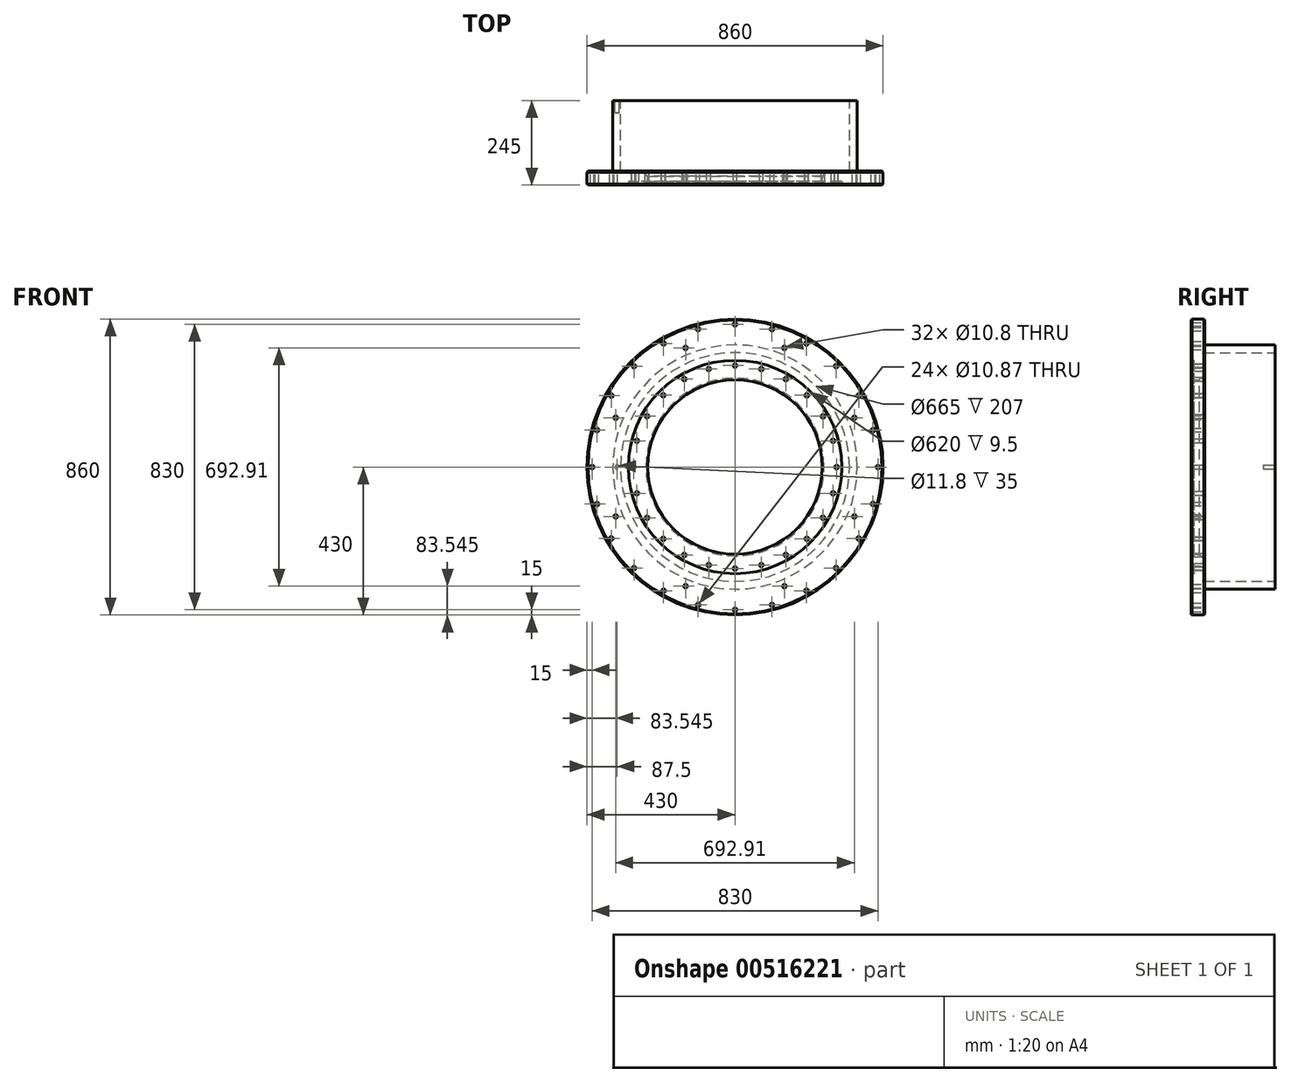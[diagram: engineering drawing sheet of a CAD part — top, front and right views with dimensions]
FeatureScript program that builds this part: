
annotation { "Feature Type Name" : "Feature", "Feature Type Description" : "" }
export const myFeature = defineFeature(function(context is Context, id is Id, definition is map)
    precondition{}
    {
        {
            var Q0;
            Q0=qCreatedBy(makeId("Front.planeOp"),FACE);
            var sketch = newSketch(context, id + "F0", { "sketchPlane" : qUnion([Q0])});
            skCircle(sketch, "E0", {"center": v(0, 0) * mm, "radius": 430 * mm});
            skCircle(sketch, "E1", {"center": v(0, 0) * mm, "radius": 250 * mm});
            skSolve(sketch);
        }
        {
            var Q0;
            Q0 = qSketchRegion(id + "F0", true);
            extrude(context, id + "F1", {"entities" : qUnion([Q0]), "depth" : 245 * mm, "offsetDistance" : 25 * mm});
        }
        {
            var Q0;
            Q0=makeQuery(id+"F1.opExtrude","CAP_FACE",FACE,{"disambiguationData":[OSD([sQuery(id+"F0.wireOp",EDGE,"E0"),sQuery(id+"F0.wireOp",EDGE,"E1")])],"isStart":true});
            var sketch = newSketch(context, id + "F2", { "sketchPlane" : qUnion([Q0])});
            skCircle(sketch, "E2", {"center": v(0, 0) * mm, "radius": 355 * mm});
            skCircle(sketch, "E3", {"center": v(0, 0) * mm, "radius": 514.3 * mm});
            skSolve(sketch);
        }
        {
            var Q0;
            Q0=makeQuery(id+"F2.imprint","IMPRINT",FACE,{"disambiguationData":[TD([[makeQuery(id+"F2.imprint","IMPRINT",EDGE,{"derivedFrom":sQuery(id+"F2.wireOp",EDGE,"E2")}),-1.0]])]});
            var Q1;
            Q1=makeQuery(id+"F2.imprint","IMPRINT",FACE,{"disambiguationData":[TD([[makeQuery(id+"F2.imprint","IMPRINT",EDGE,{"derivedFrom":sQuery(id+"F2.wireOp",EDGE,"E3")}),1.0]])]});
            extrude(context, id + "F3", {"entities" : qUnion([Q0, Q1]), "operationType" : NewBodyOperationType.REMOVE, "oppositeDirection" : true, "depth" : 205 * mm, "offsetDistance" : 25 * mm});
        }
        {
            var Q0;
            Q0=makeQuery(id+"F1.opExtrude","CAP_FACE",FACE,{"disambiguationData":[OSD([sQuery(id+"F0.wireOp",EDGE,"E0"),sQuery(id+"F0.wireOp",EDGE,"E1")])],"isStart":true});
            var sketch = newSketch(context, id + "F4", { "sketchPlane" : qUnion([Q0])});
            skCircle(sketch, "E4", {"center": v(0, 0) * mm, "radius": 332.5 * mm});
            skCircle(sketch, "E5", {"center": v(0, 0) * mm, "radius": 222.4 * mm});
            skSolve(sketch);
        }
        {
            var Q0;
            Q0=makeQuery(id+"F4.imprint","IMPRINT",FACE,{"disambiguationData":[TD([[makeQuery(id+"F4.imprint","IMPRINT",EDGE,{"derivedFrom":sQuery(id+"F4.wireOp",EDGE,"E5")}),-1.0]])]});
            var Q1;
            Q1=makeQuery(id+"F4.imprint","IMPRINT",FACE,{"disambiguationData":[TD([[makeQuery(id+"F4.imprint","IMPRINT",EDGE,{"derivedFrom":sQuery(id+"F4.wireOp",EDGE,"E4")}),1.0]])]});
            extrude(context, id + "F5", {"entities" : qUnion([Q0, Q1]), "operationType" : NewBodyOperationType.REMOVE, "oppositeDirection" : true, "depth" : 210 * mm, "offsetDistance" : 25 * mm});
        }
        {
            var Q0;
            Q0=makeQuery(id+"F1.opExtrude","CAP_FACE",FACE,{"disambiguationData":[OSD([sQuery(id+"F0.wireOp",EDGE,"E0"),sQuery(id+"F0.wireOp",EDGE,"E1")])],"isStart":false});
            var sketch = newSketch(context, id + "F6", { "sketchPlane" : qUnion([Q0])});
            skCircle(sketch, "E6", {"center": v(0, 0) * mm, "radius": 310 * mm});
            skCircle(sketch, "E7", {"center": v(0, 0) * mm, "radius": 214.22 * mm});
            skSolve(sketch);
        }
        {
            var Q0;
            Q0 = qSketchRegion(id + "F6", true);
            extrude(context, id + "F7", {"entities" : qUnion([Q0]), "operationType" : NewBodyOperationType.REMOVE, "oppositeDirection" : true, "depth" : 10 * mm, "offsetDistance" : 25 * mm});
        }
        {
            var Q0;
            Q0=qCreatedBy(makeId("Top.planeOp"),FACE);
            var sketch = newSketch(context, id + "F8", { "sketchPlane" : qUnion([Q0])});
            skLineSegment(sketch, "E8", {"start": v(0, 0) * mm, "end": v(0, -312.02) * mm});
            skPoint(sketch, "E9", {"position": v(254.25, -220) * mm});
            skPoint(sketch, "E10", {"position": v(258, -217.25) * mm});
            skLineSegment(sketch, "E11", {"start": v(257.95, -217.85) * mm, "end": v(259.23, -203.24) * mm});
            skLineSegment(sketch, "E12", {"start": v(254.25, -220) * mm, "end": v(252.48, -253.86) * mm});
            skLineSegment(sketch, "E13", {"start": v(254.25, -220) * mm, "end": v(257.34, -218.69) * mm});
            skPoint(sketch, "E14.visualSharp", {"position": v(257.9, -218.45) * mm});
            skArc(sketch, "E14.filletArc", {"start": v(257.34, -218.69) * mm, "mid": v(257.76, -218.35) * mm, "end": v(257.95, -217.85) * mm});
            skLineSegment(sketch, "E15", {"start": v(259.23, -203.24) * mm, "end": v(236.3, -203.24) * mm});
            skLineSegment(sketch, "E16", {"start": v(236.3, -203.24) * mm, "end": v(252.48, -253.86) * mm});
            skSolve(sketch);
        }
        {
            var Q0;
            Q0 = qSketchRegion(id + "F8", true);
            var Q1;
            Q1=sQuery(id+"F8.wireOp",EDGE,"E8");
            revolve(context, id + "F9", {"operationType" : NewBodyOperationType.REMOVE, "entities" : qUnion([Q0]), "axis" : qUnion([Q1]), "revolveType" : RevolveType.FULL, "oppositeDirection" : true});
        }
        {
            var Q0;
            Q0=makeQuery(id+"F1.opExtrude","CAP_FACE",FACE,{"disambiguationData":[OSD([sQuery(id+"F0.wireOp",EDGE,"E0"),sQuery(id+"F0.wireOp",EDGE,"E1")])],"isStart":true});
            var sketch = newSketch(context, id + "F10", { "sketchPlane" : qUnion([Q0])});
            skCircle(sketch, "E17", {"center": v(342.5, 0) * mm, "radius": 5.9 * mm});
            skSolve(sketch);
        }
        {
            var Q0;
            Q0 = qSketchRegion(id + "F10", true);
            extrude(context, id + "F11", {"entities" : qUnion([Q0]), "operationType" : NewBodyOperationType.REMOVE, "oppositeDirection" : true, "depth" : 35 * mm, "offsetDistance" : 25 * mm});
        }
        {
            var Q0;
            Q0=makeQuery(id+"F3.boolean.opBoolean","COPY",FACE,{"derivedFrom":makeQuery(id+"F3.opExtrude","CAP_FACE",FACE,{"disambiguationData":[OSD([sQuery(id+"F2.wireOp",EDGE,"E2"),sQuery(id+"F2.wireOp",EDGE,"E3")])],"isStart":false})});
            var sketch = newSketch(context, id + "F12", { "sketchPlane" : qUnion([Q0])});
            skCircle(sketch, "E18", {"center": v(0, 415) * mm, "radius": 5.44 * mm});
            skCircle(sketch, "E19.1.0", {"center": v(-107.4, 400.86) * mm, "radius": 5.44 * mm});
            skCircle(sketch, "E19.2.0", {"center": v(-207.5, 359.4) * mm, "radius": 5.44 * mm});
            skCircle(sketch, "E19.3.0", {"center": v(-293.45, 293.45) * mm, "radius": 5.44 * mm});
            skCircle(sketch, "E19.4.0", {"center": v(-359.4, 207.5) * mm, "radius": 5.44 * mm});
            skCircle(sketch, "E19.5.0", {"center": v(-400.86, 107.4) * mm, "radius": 5.44 * mm});
            skCircle(sketch, "E19.6.0", {"center": v(-415, 0) * mm, "radius": 5.44 * mm});
            skCircle(sketch, "E19.7.0", {"center": v(-400.86, -107.4) * mm, "radius": 5.44 * mm});
            skCircle(sketch, "E19.8.0", {"center": v(-359.4, -207.5) * mm, "radius": 5.44 * mm});
            skCircle(sketch, "E19.9.0", {"center": v(-293.45, -293.45) * mm, "radius": 5.44 * mm});
            skCircle(sketch, "E19.10.0", {"center": v(-207.5, -359.4) * mm, "radius": 5.44 * mm});
            skCircle(sketch, "E19.11.0", {"center": v(-107.4, -400.86) * mm, "radius": 5.44 * mm});
            skCircle(sketch, "E19.12.0", {"center": v(0, -415) * mm, "radius": 5.44 * mm});
            skCircle(sketch, "E19.13.0", {"center": v(107.4, -400.86) * mm, "radius": 5.44 * mm});
            skCircle(sketch, "E19.14.0", {"center": v(207.5, -359.4) * mm, "radius": 5.44 * mm});
            skCircle(sketch, "E19.15.0", {"center": v(293.45, -293.45) * mm, "radius": 5.44 * mm});
            skCircle(sketch, "E19.16.0", {"center": v(359.4, -207.5) * mm, "radius": 5.44 * mm});
            skCircle(sketch, "E19.17.0", {"center": v(400.86, -107.4) * mm, "radius": 5.44 * mm});
            skCircle(sketch, "E19.18.0", {"center": v(415, 0) * mm, "radius": 5.44 * mm});
            skCircle(sketch, "E19.19.0", {"center": v(400.86, 107.4) * mm, "radius": 5.44 * mm});
            skCircle(sketch, "E19.20.0", {"center": v(359.4, 207.5) * mm, "radius": 5.44 * mm});
            skCircle(sketch, "E19.21.0", {"center": v(293.45, 293.45) * mm, "radius": 5.44 * mm});
            skCircle(sketch, "E19.22.0", {"center": v(207.5, 359.4) * mm, "radius": 5.44 * mm});
            skCircle(sketch, "E19.23.0", {"center": v(107.4, 400.86) * mm, "radius": 5.44 * mm});
            skPoint(sketch, "E19.center", {"position": v(0, 0) * mm});
            skSolve(sketch);
        }
        {
            var Q0;
            Q0 = qSketchRegion(id + "F12", true);
            extrude(context, id + "F13", {"entities" : qUnion([Q0]), "operationType" : NewBodyOperationType.REMOVE, "oppositeDirection" : true, "depth" : 100 * mm, "offsetDistance" : 25 * mm});
        }
        {
            var Q0;
            Q0=makeQuery(id+"F5.boolean.opBoolean","COPY",FACE,{"derivedFrom":makeQuery(id+"F5.opExtrude","CAP_FACE",FACE,{"disambiguationData":[OSD([sQuery(id+"F4.wireOp",EDGE,"E4"),sQuery(id+"F4.wireOp",EDGE,"E5")])],"isStart":false})});
            var sketch = newSketch(context, id + "F14", { "sketchPlane" : qUnion([Q0])});
            skCircle(sketch, "E20", {"center": v(0, 295) * mm, "radius": 5.4 * mm});
            skCircle(sketch, "E21.1.0", {"center": v(-76.35, 284.95) * mm, "radius": 5.4 * mm});
            skCircle(sketch, "E21.2.0", {"center": v(-147.5, 255.48) * mm, "radius": 5.4 * mm});
            skCircle(sketch, "E21.3.0", {"center": v(-208.6, 208.6) * mm, "radius": 5.4 * mm});
            skCircle(sketch, "E21.4.0", {"center": v(-255.48, 147.5) * mm, "radius": 5.4 * mm});
            skCircle(sketch, "E21.5.0", {"center": v(-284.95, 76.35) * mm, "radius": 5.4 * mm});
            skCircle(sketch, "E21.6.0", {"center": v(-295, 0) * mm, "radius": 5.4 * mm});
            skCircle(sketch, "E21.7.0", {"center": v(-284.95, -76.35) * mm, "radius": 5.4 * mm});
            skCircle(sketch, "E21.8.0", {"center": v(-255.48, -147.5) * mm, "radius": 5.4 * mm});
            skCircle(sketch, "E21.9.0", {"center": v(-208.6, -208.6) * mm, "radius": 5.4 * mm});
            skCircle(sketch, "E21.10.0", {"center": v(-147.5, -255.48) * mm, "radius": 5.4 * mm});
            skCircle(sketch, "E21.11.0", {"center": v(-76.35, -284.95) * mm, "radius": 5.4 * mm});
            skCircle(sketch, "E21.12.0", {"center": v(0, -295) * mm, "radius": 5.4 * mm});
            skCircle(sketch, "E21.13.0", {"center": v(76.35, -284.95) * mm, "radius": 5.4 * mm});
            skCircle(sketch, "E21.14.0", {"center": v(147.5, -255.48) * mm, "radius": 5.4 * mm});
            skCircle(sketch, "E21.15.0", {"center": v(208.6, -208.6) * mm, "radius": 5.4 * mm});
            skCircle(sketch, "E21.16.0", {"center": v(255.48, -147.5) * mm, "radius": 5.4 * mm});
            skCircle(sketch, "E21.17.0", {"center": v(284.95, -76.35) * mm, "radius": 5.4 * mm});
            skCircle(sketch, "E21.18.0", {"center": v(295, 0) * mm, "radius": 5.4 * mm});
            skCircle(sketch, "E21.19.0", {"center": v(284.95, 76.35) * mm, "radius": 5.4 * mm});
            skCircle(sketch, "E21.20.0", {"center": v(255.48, 147.5) * mm, "radius": 5.4 * mm});
            skCircle(sketch, "E21.21.0", {"center": v(208.6, 208.6) * mm, "radius": 5.4 * mm});
            skCircle(sketch, "E21.22.0", {"center": v(147.5, 255.48) * mm, "radius": 5.4 * mm});
            skCircle(sketch, "E21.23.0", {"center": v(76.35, 284.95) * mm, "radius": 5.4 * mm});
            skPoint(sketch, "E21.center", {"position": v(0, 0) * mm});
            skSolve(sketch);
        }
        {
            var Q0;
            Q0 = qSketchRegion(id + "F14", true);
            extrude(context, id + "F15", {"entities" : qUnion([Q0]), "operationType" : NewBodyOperationType.REMOVE, "oppositeDirection" : true, "depth" : 331 * mm, "offsetDistance" : 25 * mm});
        }
        {
            var Q0;
            Q0=makeQuery(id+"F3.boolean.opBoolean","COPY",FACE,{"derivedFrom":makeQuery(id+"F3.opExtrude","CAP_FACE",FACE,{"disambiguationData":[OSD([sQuery(id+"F2.wireOp",EDGE,"E2"),sQuery(id+"F2.wireOp",EDGE,"E3")])],"isStart":false})});
            var sketch = newSketch(context, id + "F16", { "sketchPlane" : qUnion([Q0])});
            skCircle(sketch, "E22", {"center": v(-143.5, 346.45) * mm, "radius": 5.4 * mm});
            skCircle(sketch, "E23.1.0", {"center": v(-346.45, 143.5) * mm, "radius": 5.4 * mm});
            skCircle(sketch, "E23.2.0", {"center": v(-346.45, -143.5) * mm, "radius": 5.4 * mm});
            skCircle(sketch, "E23.3.0", {"center": v(-143.5, -346.45) * mm, "radius": 5.4 * mm});
            skCircle(sketch, "E23.4.0", {"center": v(143.5, -346.45) * mm, "radius": 5.4 * mm});
            skCircle(sketch, "E23.5.0", {"center": v(346.45, -143.5) * mm, "radius": 5.4 * mm});
            skCircle(sketch, "E23.6.0", {"center": v(346.45, 143.5) * mm, "radius": 5.4 * mm});
            skCircle(sketch, "E23.7.0", {"center": v(143.5, 346.45) * mm, "radius": 5.4 * mm});
            skPoint(sketch, "E23.center", {"position": v(0, 0) * mm});
            skSolve(sketch);
        }
        {
            var Q0;
            Q0 = qSketchRegion(id + "F16", true);
            extrude(context, id + "F17", {"entities" : qUnion([Q0]), "operationType" : NewBodyOperationType.REMOVE, "oppositeDirection" : true, "depth" : 50 * mm, "offsetDistance" : 25 * mm});
        }
        {
            var Q0;
            Q0=makeQuery(id+"F5.boolean.opBoolean","COPY",EDGE,{"derivedFrom":makeQuery(id+"F5.opExtrude","CAP_EDGE",EDGE,{"disambiguationData":[OSD([sQuery(id+"F4.wireOp",EDGE,"E4")])],"isStart":false})});
            fillet(context, id + "F18", {"entities" : qUnion([Q0]), "radius" : 3 * mm, "tangentPropagation" : true, "allowEdgeOverflow" : false});
        }
        {
            var Q0;
            Q0=makeQuery(id+"F1.opExtrude","CAP_EDGE",EDGE,{"disambiguationData":[OSD([sQuery(id+"F0.wireOp",EDGE,"E0")])],"isStart":false});
            var Q1;
            Q1=makeQuery(id+"F3.boolean.opBoolean","INTERSECT",EDGE,{"derivedFrom":[makeQuery(id+"F1.opExtrude","SWEPT_FACE",FACE,{"disambiguationData":[OSD([sQuery(id+"F0.wireOp",EDGE,"E0")])]}),makeQuery(id+"F3.opExtrude","CAP_FACE",FACE,{"disambiguationData":[OSD([sQuery(id+"F2.wireOp",EDGE,"E2"),sQuery(id+"F2.wireOp",EDGE,"E3")])],"isStart":false})]});
            chamfer(context, id + "F19", {"entities" : qUnion([Q0, Q1]), "width" : 3 * mm, "tangentPropagation" : true});
        }
        {
            var Q0;
            Q0=makeQuery(id+"F3.boolean.opBoolean","COPY",EDGE,{"derivedFrom":makeQuery(id+"F3.opExtrude","CAP_EDGE",EDGE,{"disambiguationData":[OSD([sQuery(id+"F2.wireOp",EDGE,"E2")])],"isStart":false})});
            fillet(context, id + "F20", {"entities" : qUnion([Q0]), "radius" : 4 * mm, "tangentPropagation" : true, "allowEdgeOverflow" : false});
        }
        {
            var Q0;
            Q0=makeQuery(id+"F7.boolean.opBoolean","COPY",EDGE,{"derivedFrom":makeQuery(id+"F7.opExtrude","CAP_EDGE",EDGE,{"disambiguationData":[OSD([sQuery(id+"F6.wireOp",EDGE,"E6")])],"isStart":false})});
            fillet(context, id + "F21", {"entities" : qUnion([Q0]), "radius" : .5 * mm, "tangentPropagation" : true, "allowEdgeOverflow" : false});
        }
    });
